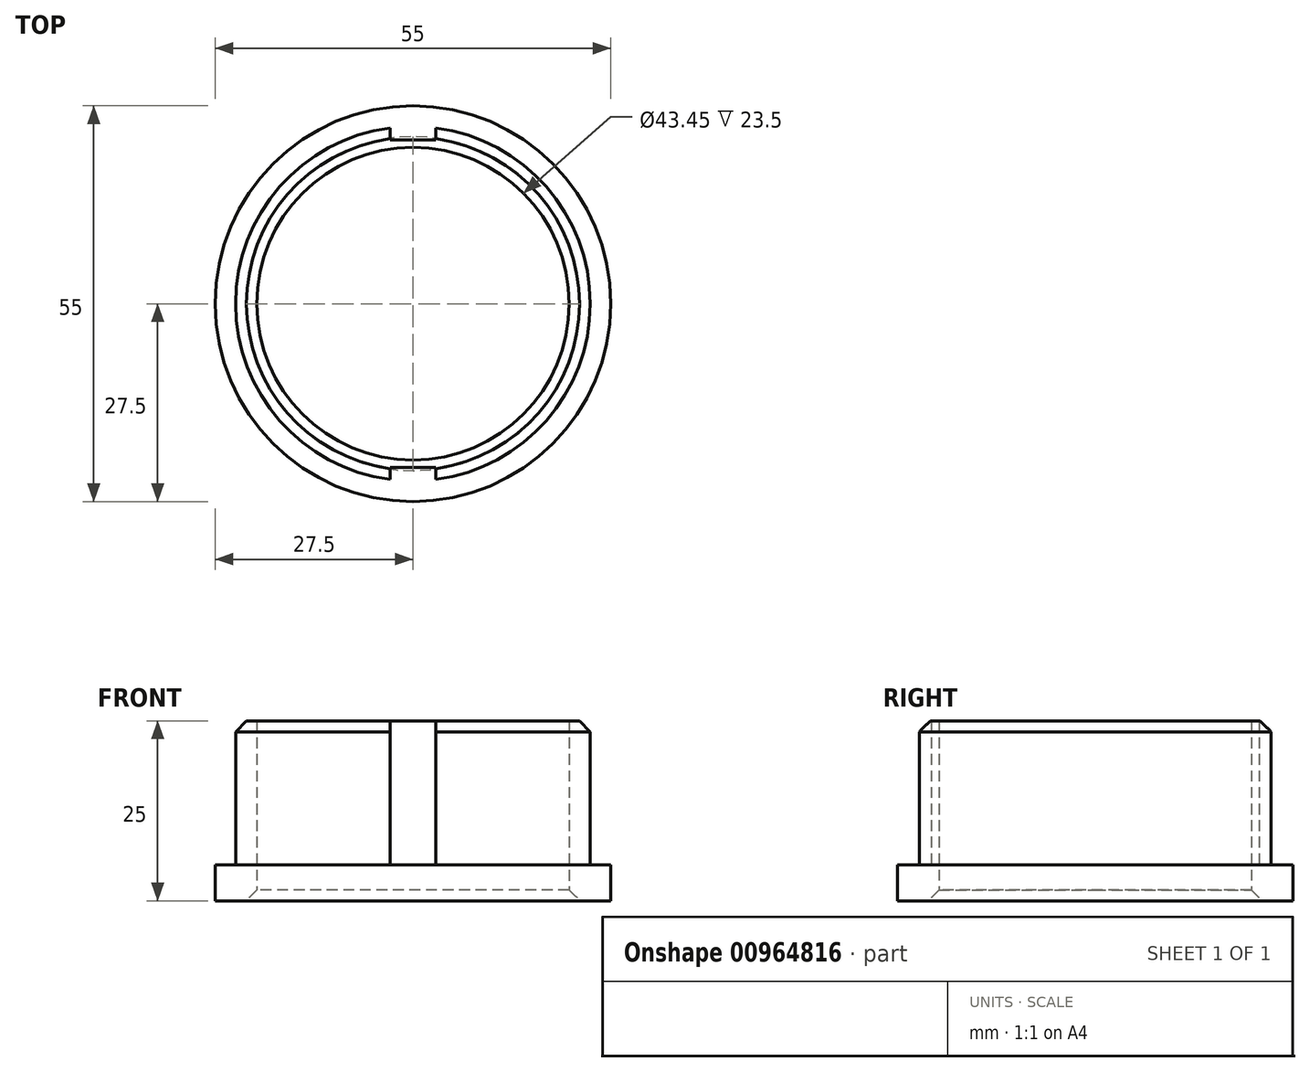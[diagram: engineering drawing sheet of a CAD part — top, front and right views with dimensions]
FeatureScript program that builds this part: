
annotation { "Feature Type Name" : "Feature", "Feature Type Description" : "" }
export const myFeature = defineFeature(function(context is Context, id is Id, definition is map)
    precondition{}
    {
        {
            var Q0;
            Q0=qCreatedBy(makeId("Top.planeOp"),FACE);
            var sketch = newSketch(context, id + "F0", { "sketchPlane" : qUnion([Q0])});
            skArc(sketch, "E0", {"start": v(-3.2, 24.44) * mm, "mid": v(-24.65, 0) * mm, "end": v(-3.2, -24.44) * mm});
            skCircle(sketch, "E1", {"center": v(0, 0) * mm, "radius": 27.5 * mm});
            skLineSegment(sketch, "E2", {"start": v(0, 27.5) * mm, "end": v(0, -27.5) * mm, "construction": true});
            skLineSegment(sketch, "E3", {"start": v(-3.2, 24.44) * mm, "end": v(-3.2, 22.78) * mm});
            skLineSegment(sketch, "E4", {"start": v(-3.2, 22.78) * mm, "end": v(3.2, 22.78) * mm});
            skLineSegment(sketch, "E5", {"start": v(3.2, 22.78) * mm, "end": v(3.2, 24.44) * mm});
            skLineSegment(sketch, "E6.MirrorCS", {"start": v(-3.2, -24.44) * mm, "end": v(-3.2, -22.78) * mm});
            skLineSegment(sketch, "E7.MirrorCS", {"start": v(3.2, -22.78) * mm, "end": v(3.2, -24.44) * mm});
            skLineSegment(sketch, "E8.MirrorCS", {"start": v(-3.2, -22.78) * mm, "end": v(3.2, -22.78) * mm});
            skArc(sketch, "E9.trimOffspring", {"start": v(3.2, -24.44) * mm, "mid": v(24.65, 0) * mm, "end": v(3.2, 24.44) * mm});
            skCircle(sketch, "E10", {"center": v(0, 0) * mm, "radius": 21.72 * mm});
            skSolve(sketch);
        }
        {
            var Q0;
            Q0=makeQuery(id+"F0.imprint","IMPRINT",FACE,{"disambiguationData":[TD([[makeQuery(id+"F0.imprint","IMPRINT",EDGE,{"derivedFrom":sQuery(id+"F0.wireOp",EDGE,"E0")}),1.0]])]});
            extrude(context, id + "F1", {"entities" : qUnion([Q0]), "depth" : 25 * mm, "offsetDistance" : 25 * mm});
        }
        {
            var Q0;
            Q0=makeQuery(id+"F0.imprint","IMPRINT",FACE,{"disambiguationData":[TD([[makeQuery(id+"F0.imprint","IMPRINT",EDGE,{"derivedFrom":sQuery(id+"F0.wireOp",EDGE,"E0")}),-1.0]])]});
            extrude(context, id + "F2", {"entities" : qUnion([Q0]), "operationType" : NewBodyOperationType.ADD, "depth" : 5 * mm, "offsetDistance" : 25 * mm});
        }
        {
            var Q0;
            Q0=makeQuery(id+"F1.opExtrude","CAP_EDGE",EDGE,{"disambiguationData":[OSD([sQuery(id+"F0.wireOp",EDGE,"E0")])],"isStart":false});
            var Q1;
            Q1=makeQuery(id+"F1.opExtrude","CAP_EDGE",EDGE,{"disambiguationData":[OSD([sQuery(id+"F0.wireOp",EDGE,"E9.trimOffspring")])],"isStart":false});
            var Q2;
            Q2=makeQuery(id+"F1.opExtrude","CAP_EDGE",EDGE,{"disambiguationData":[OSD([sQuery(id+"F0.wireOp",EDGE,"c1xwIZaP-ZA5b-PFj9-Me3j-MZ56enI3r4Q8")])],"isStart":true});
            var Q3;
            Q3=makeQuery(id+"F1.opExtrude","CAP_EDGE",EDGE,{"disambiguationData":[OSD([sQuery(id+"F0.wireOp",EDGE,"fc1b8e0b-e1a0-4eff-aef7-98e39e9f1fd9.trimOffspring")])],"isStart":true});
            var Q4;
            Q4=makeQuery(id+"F1.opExtrude","CAP_EDGE",EDGE,{"disambiguationData":[OSD([sQuery(id+"F0.wireOp",EDGE,"hKKh9wnK-Clvy-EVve-ayxq-jaVVNss7U9dz")])],"isStart":true});
            var Q5;
            Q5=makeQuery(id+"F1.opExtrude","CAP_EDGE",EDGE,{"disambiguationData":[OSD([sQuery(id+"F0.wireOp",EDGE,"TywvqC7i-z6qB-jQbj-9tB0-LES4fyUz0PsG")])],"isStart":true});
            var Q6;
            Q6=makeQuery(id+"F1.opExtrude","CAP_EDGE",EDGE,{"disambiguationData":[OSD([sQuery(id+"F0.wireOp",EDGE,"E10")])],"isStart":true});
            chamfer(context, id + "F3", {"entities" : qUnion([Q0, Q1, Q2, Q3, Q4, Q5, Q6]), "width" : 1.5 * mm, "tangentPropagation" : true});
        }
    });
